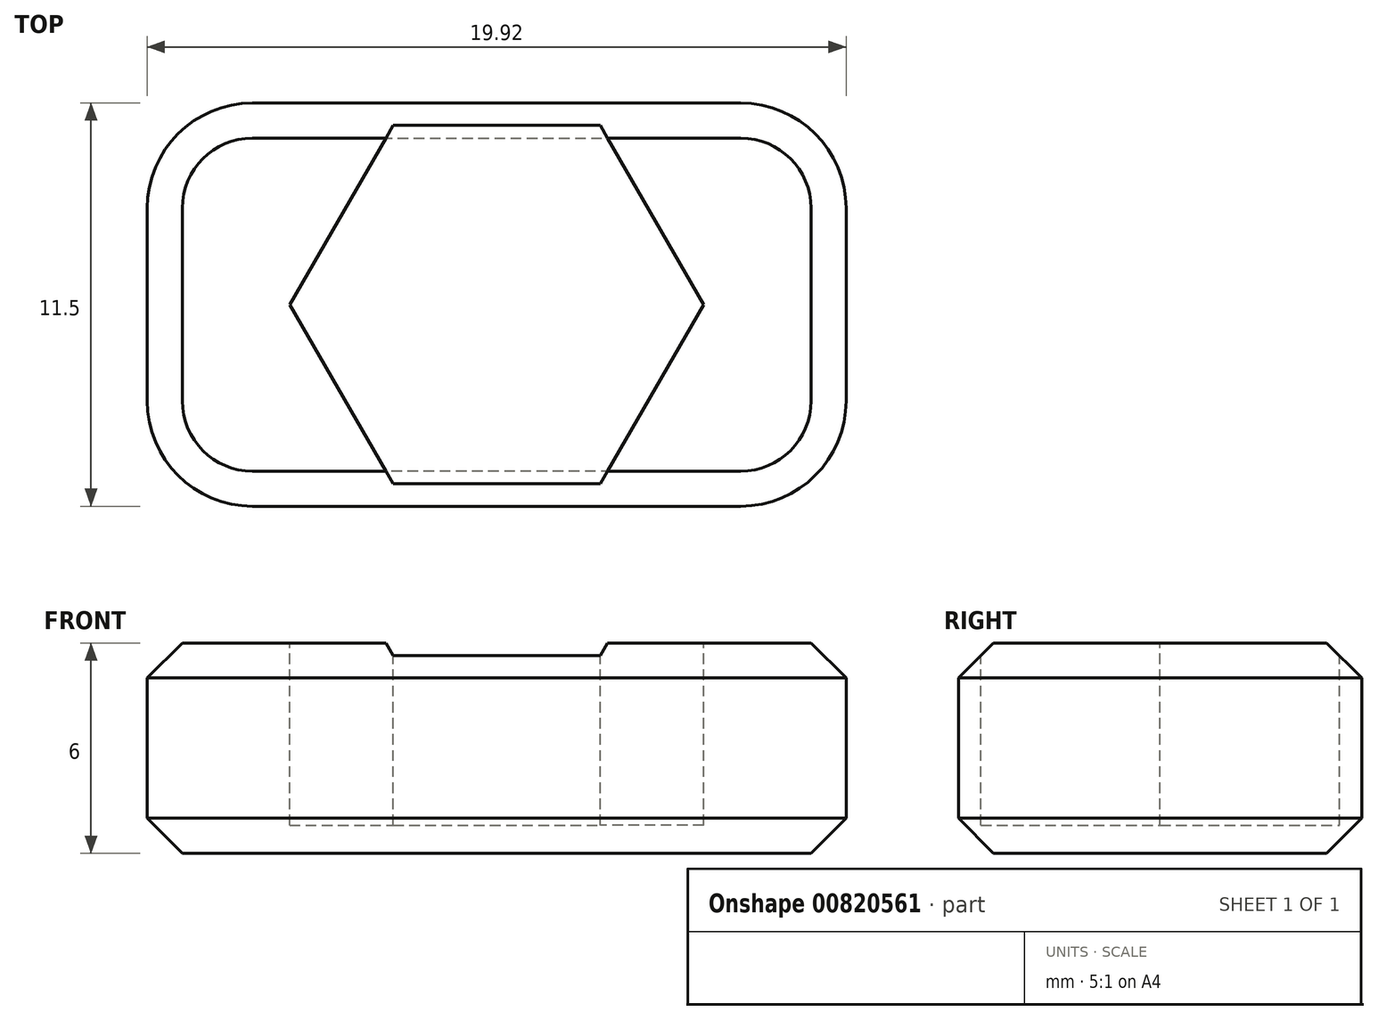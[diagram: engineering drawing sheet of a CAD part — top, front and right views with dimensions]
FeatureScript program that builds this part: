
annotation { "Feature Type Name" : "Feature", "Feature Type Description" : "" }
export const myFeature = defineFeature(function(context is Context, id is Id, definition is map)
    precondition{}
    {
        {
            var Q0;
            Q0=qCreatedBy(makeId("Top.planeOp"),FACE);
            var sketch = newSketch(context, id + "F0", { "sketchPlane" : qUnion([Q0])});
            skLineSegment(sketch, "E0.bottom", {"start": v(-6.96, 5.75) * mm, "end": v(6.96, 5.75) * mm});
            skLineSegment(sketch, "E0.top", {"start": v(-6.96, -5.75) * mm, "end": v(6.96, -5.75) * mm});
            skLineSegment(sketch, "E0.left", {"start": v(-9.96, 2.75) * mm, "end": v(-9.96, -2.75) * mm});
            skLineSegment(sketch, "E0.right", {"start": v(9.96, 2.75) * mm, "end": v(9.96, -2.75) * mm});
            skPoint(sketch, "E0.middle", {"position": v(0, 0) * mm});
            skPoint(sketch, "E1.visualSharp", {"position": v(-9.96, 5.75) * mm});
            skArc(sketch, "E1.filletArc", {"start": v(-6.96, 5.75) * mm, "mid": v(-9.08, 4.87) * mm, "end": v(-9.96, 2.75) * mm});
            skPoint(sketch, "E2.visualSharp", {"position": v(9.96, 5.75) * mm});
            skArc(sketch, "E2.filletArc", {"start": v(9.96, 2.75) * mm, "mid": v(9.08, 4.87) * mm, "end": v(6.96, 5.75) * mm});
            skPoint(sketch, "E3.visualSharp", {"position": v(9.96, -5.75) * mm});
            skArc(sketch, "E3.filletArc", {"start": v(6.96, -5.75) * mm, "mid": v(9.08, -4.87) * mm, "end": v(9.96, -2.75) * mm});
            skPoint(sketch, "E4.visualSharp", {"position": v(-9.96, -5.75) * mm});
            skArc(sketch, "E4.filletArc", {"start": v(-9.96, -2.75) * mm, "mid": v(-9.08, -4.87) * mm, "end": v(-6.96, -5.75) * mm});
            skSolve(sketch);
        }
        {
            var Q0;
            Q0=makeQuery(id+"F0.imprint","IMPRINT",FACE,{"disambiguationData":[TD([[makeQuery(id+"F0.imprint","IMPRINT",EDGE,{"derivedFrom":sQuery(id+"F0.wireOp",EDGE,"E0.bottom")}),-1.0]])]});
            extrude(context, id + "F1", {"entities" : qUnion([Q0]), "depth" : 6 * mm, "offsetDistance" : 25 * mm});
        }
        {
            var Q0;
            Q0=makeQuery(id+"F1.opExtrude","CAP_FACE",FACE,{"disambiguationData":[OSD([sQuery(id+"F0.wireOp",EDGE,"E0.bottom"),sQuery(id+"F0.wireOp",EDGE,"E0.top"),sQuery(id+"F0.wireOp",EDGE,"E0.left"),sQuery(id+"F0.wireOp",EDGE,"E0.right"),sQuery(id+"F0.wireOp",EDGE,"E1.filletArc"),sQuery(id+"F0.wireOp",EDGE,"E2.filletArc"),sQuery(id+"F0.wireOp",EDGE,"E3.filletArc"),sQuery(id+"F0.wireOp",EDGE,"E4.filletArc")])],"isStart":false});
            var sketch = newSketch(context, id + "F2", { "sketchPlane" : qUnion([Q0])});
            skCircle(sketch, "E5.cCircle", {"center": v(0, 0) * mm, "radius": 5.9 * mm, "construction": true});
            skLineSegment(sketch, "E5.0", {"start": v(-2.95, 5.1) * mm, "end": v(2.95, 5.1) * mm});
            skLineSegment(sketch, "E5.1", {"start": v(2.95, 5.1) * mm, "end": v(5.9, 0) * mm});
            skLineSegment(sketch, "E5.2", {"start": v(5.9, 0) * mm, "end": v(2.95, -5.1) * mm});
            skLineSegment(sketch, "E5.3", {"start": v(2.95, -5.1) * mm, "end": v(-2.95, -5.1) * mm});
            skLineSegment(sketch, "E5.4", {"start": v(-2.95, -5.1) * mm, "end": v(-5.9, 0) * mm});
            skLineSegment(sketch, "E5.5", {"start": v(-5.9, 0) * mm, "end": v(-2.95, 5.1) * mm});
            skSolve(sketch);
        }
        {
            var Q0;
            Q0=makeQuery(id+"F2.imprint","IMPRINT",FACE,{"disambiguationData":[TD([[makeQuery(id+"F2.imprint","IMPRINT",EDGE,{"derivedFrom":sQuery(id+"F2.wireOp",EDGE,"E5.0")}),-1.0]])]});
            extrude(context, id + "F3", {"entities" : qUnion([Q0]), "operationType" : NewBodyOperationType.REMOVE, "oppositeDirection" : true, "depth" : 5.2 * mm, "offsetDistance" : 25 * mm});
        }
        {
            var Q0;
            Q0=makeQuery(id+"F1.opExtrude","CAP_EDGE",EDGE,{"disambiguationData":[OSD([sQuery(id+"F0.wireOp",EDGE,"E0.bottom")])],"isStart":false});
            var Q1;
            Q1=makeQuery(id+"F1.opExtrude","CAP_EDGE",EDGE,{"disambiguationData":[OSD([sQuery(id+"F0.wireOp",EDGE,"E0.bottom")])],"isStart":true});
            chamfer(context, id + "F4", {"entities" : qUnion([Q0, Q1]), "width" : 1 * mm, "tangentPropagation" : true});
        }
    });
